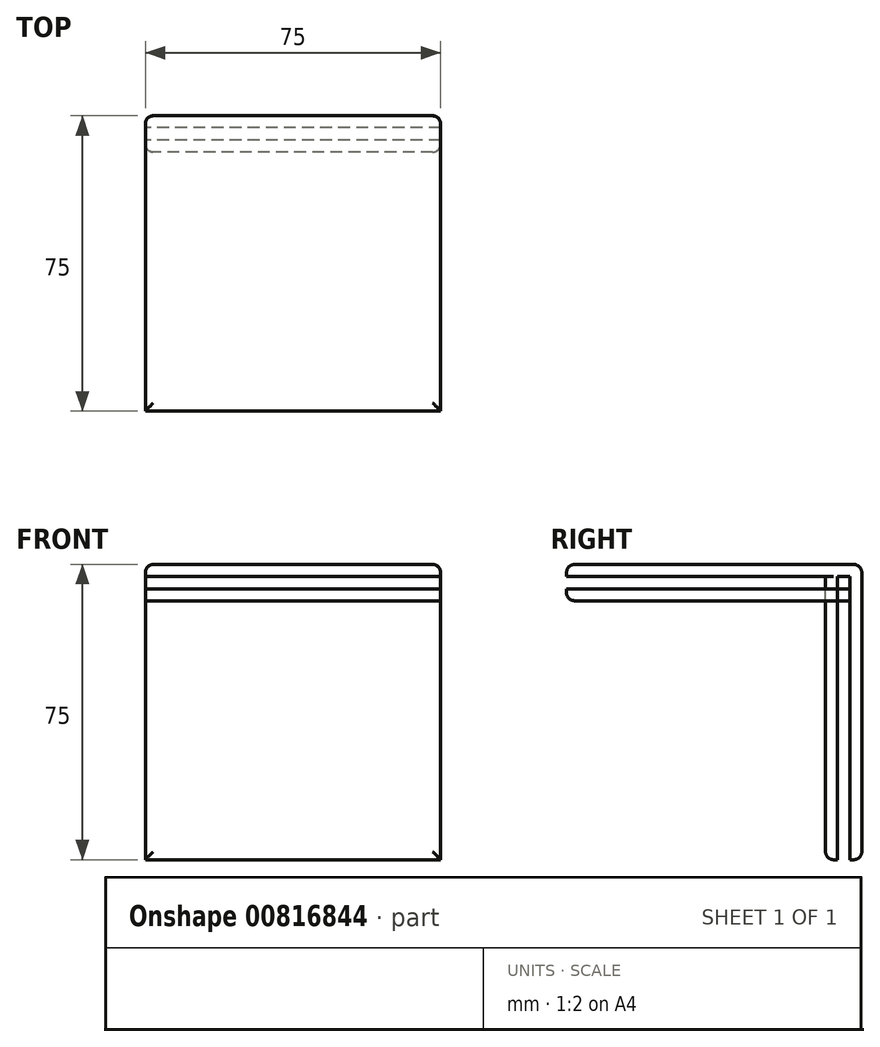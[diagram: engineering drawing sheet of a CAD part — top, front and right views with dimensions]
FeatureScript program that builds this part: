
annotation { "Feature Type Name" : "Feature", "Feature Type Description" : "" }
export const myFeature = defineFeature(function(context is Context, id is Id, definition is map)
    precondition{}
    {
        {
            var Q0;
            Q0=qCreatedBy(makeId("Top.planeOp"),FACE);
            var sketch = newSketch(context, id + "F0", { "sketchPlane" : qUnion([Q0])});
            skLineSegment(sketch, "E0.bottom", {"start": v(37.5, -37.5) * mm, "end": v(-37.5, -37.5) * mm});
            skLineSegment(sketch, "E0.top", {"start": v(37.5, 37.5) * mm, "end": v(-37.5, 37.5) * mm});
            skLineSegment(sketch, "E0.left", {"start": v(37.5, -37.5) * mm, "end": v(37.5, 37.5) * mm});
            skLineSegment(sketch, "E0.right", {"start": v(-37.5, -37.5) * mm, "end": v(-37.5, 37.5) * mm});
            skPoint(sketch, "E0.middle", {"position": v(0, 0) * mm});
            skSolve(sketch);
        }
        {
            var Q0;
            Q0=qSketchRegion(id+"F0",true);
            extrude(context, id + "F1", {"entities" : qUnion([Q0]), "depth" : 3 * mm, "offsetDistance" : 25 * mm});
        }
        {
            var Q0;
            Q0=makeQuery(id+"F1.opExtrude","SWEPT_FACE",FACE,{"disambiguationData":[OSD([sQuery(id+"F0.wireOp",EDGE,"E0.right")])]});
            var sketch = newSketch(context, id + "F2", { "sketchPlane" : qUnion([Q0])});
            skLineSegment(sketch, "E1.bottom", {"start": v(-37.5, 3) * mm, "end": v(-34.5, 3) * mm});
            skLineSegment(sketch, "E1.top", {"start": v(-37.5, -72) * mm, "end": v(-34.5, -72) * mm});
            skLineSegment(sketch, "E1.left", {"start": v(-37.5, 3) * mm, "end": v(-37.5, -72) * mm});
            skLineSegment(sketch, "E1.right", {"start": v(-34.5, 3) * mm, "end": v(-34.5, -72) * mm});
            skLineSegment(sketch, "E2.bottom", {"start": v(-31.3, 3) * mm, "end": v(-28.3, 3) * mm});
            skLineSegment(sketch, "E2.top", {"start": v(-31.3, -72) * mm, "end": v(-28.3, -72) * mm});
            skLineSegment(sketch, "E2.left", {"start": v(-31.3, 3) * mm, "end": v(-31.3, -72) * mm});
            skLineSegment(sketch, "E2.right", {"start": v(-28.3, 3) * mm, "end": v(-28.3, -72) * mm});
            skLineSegment(sketch, "E3", {"start": v(-36, -72) * mm, "end": v(-7.39, -72) * mm, "construction": true});
            skSolve(sketch);
        }
        {
            var Q0;
            Q0=qSketchRegion(id+"F2",true);
            var Q1;
            Q1=makeQuery(id+"F1.opExtrude","SWEPT_FACE",FACE,{"disambiguationData":[OSD([sQuery(id+"F0.wireOp",EDGE,"E0.left")])]});
            extrude(context, id + "F3", {"entities" : qUnion([Q0]), "operationType" : NewBodyOperationType.ADD, "endBound" : BoundingType.UP_TO_SURFACE, "oppositeDirection" : true, "depth" : 25 * mm, "endBoundEntityFace" : qUnion([Q1]), "offsetDistance" : 25 * mm});
        }
        {
            var Q0;
            Q0=makeQuery(id+"F1.opExtrude","SWEPT_FACE",FACE,{"disambiguationData":[OSD([sQuery(id+"F0.wireOp",EDGE,"E0.bottom")])]});
            var sketch = newSketch(context, id + "F4", { "sketchPlane" : qUnion([Q0])});
            skLineSegment(sketch, "E4.0", {"start": v(37.5, -3.2) * mm, "end": v(-37.5, -3.2) * mm});
            skLineSegment(sketch, "E5.bottom", {"start": v(-37.5, -3.2) * mm, "end": v(37.5, -3.2) * mm});
            skLineSegment(sketch, "E5.top", {"start": v(-37.5, -6.2) * mm, "end": v(37.5, -6.2) * mm});
            skLineSegment(sketch, "E5.left", {"start": v(-37.5, -3.2) * mm, "end": v(-37.5, -6.2) * mm});
            skLineSegment(sketch, "E5.right", {"start": v(37.5, -3.2) * mm, "end": v(37.5, -6.2) * mm});
            skLineSegment(sketch, "E6.0", {"start": v(37.5, -72) * mm, "end": v(37.5, -3.2) * mm});
            skSolve(sketch);
        }
        {
            var Q0;
            Q0=qSketchRegion(id+"F4",true);
            var Q1;
            Q1=makeQuery(id+"F3.opExtrude","SWEPT_FACE",FACE,{"disambiguationData":[OSD([sQuery(id+"F2.wireOp",EDGE,"E1.right")])]});
            extrude(context, id + "F5", {"entities" : qUnion([Q0]), "endBound" : BoundingType.UP_TO_SURFACE, "oppositeDirection" : true, "depth" : 25 * mm, "endBoundEntityFace" : qUnion([Q1]), "offsetDistance" : 25 * mm});
        }
        {
            var Q0;
            Q0=makeQuery(id+"F3.boolean.opBoolean","MERGE",FACE,{"derivedFrom":[makeQuery(id+"F1.opExtrude","SWEPT_FACE",FACE,{"disambiguationData":[OSD([sQuery(id+"F0.wireOp",EDGE,"E0.right")])]}),makeQuery(id+"F3.opExtrude","CAP_FACE",FACE,{"disambiguationData":[OSD([sQuery(id+"F2.wireOp",EDGE,"E1.bottom"),sQuery(id+"F2.wireOp",EDGE,"E1.top"),sQuery(id+"F2.wireOp",EDGE,"E1.left"),sQuery(id+"F2.wireOp",EDGE,"E1.right")])],"isStart":true}),makeQuery(id+"F3.opExtrude","CAP_FACE",FACE,{"disambiguationData":[OSD([sQuery(id+"F2.wireOp",EDGE,"E2.bottom"),sQuery(id+"F2.wireOp",EDGE,"E2.top"),sQuery(id+"F2.wireOp",EDGE,"E2.left"),sQuery(id+"F2.wireOp",EDGE,"E2.right")])],"isStart":true})]});
            var sketch = newSketch(context, id + "F6", { "sketchPlane" : qUnion([Q0])});
            skLineSegment(sketch, "E7.0", {"start": v(-34.5, -3.2) * mm, "end": v(37.5, -3.2) * mm});
            skLineSegment(sketch, "E8.bottom", {"start": v(-34.5, 0) * mm, "end": v(-31.3, 0) * mm});
            skLineSegment(sketch, "E8.top", {"start": v(-34.5, -3.2) * mm, "end": v(-31.3, -3.2) * mm});
            skLineSegment(sketch, "E8.left", {"start": v(-34.5, 0) * mm, "end": v(-34.5, -3.2) * mm});
            skLineSegment(sketch, "E8.right", {"start": v(-31.3, 0) * mm, "end": v(-31.3, -3.2) * mm});
            skSolve(sketch);
        }
        {
            var Q0;
            Q0=qSketchRegion(id+"F6",true);
            var Q1;
            Q1=makeQuery(id+"F3.boolean.opBoolean","MERGE",FACE,{"derivedFrom":[makeQuery(id+"F1.opExtrude","SWEPT_FACE",FACE,{"disambiguationData":[OSD([sQuery(id+"F0.wireOp",EDGE,"E0.left")])]}),makeQuery(id+"F3.opExtrude","CAP_FACE",FACE,{"disambiguationData":[OSD([sQuery(id+"F2.wireOp",EDGE,"E1.bottom"),sQuery(id+"F2.wireOp",EDGE,"E1.top"),sQuery(id+"F2.wireOp",EDGE,"E1.left"),sQuery(id+"F2.wireOp",EDGE,"E1.right")])],"isStart":false}),makeQuery(id+"F3.opExtrude","CAP_FACE",FACE,{"disambiguationData":[OSD([sQuery(id+"F2.wireOp",EDGE,"E2.bottom"),sQuery(id+"F2.wireOp",EDGE,"E2.top"),sQuery(id+"F2.wireOp",EDGE,"E2.left"),sQuery(id+"F2.wireOp",EDGE,"E2.right")])],"isStart":false})]});
            extrude(context, id + "F7", {"entities" : qUnion([Q0]), "endBound" : BoundingType.UP_TO_SURFACE, "oppositeDirection" : true, "depth" : 25 * mm, "endBoundEntityFace" : qUnion([Q1]), "offsetDistance" : 25 * mm});
        }
        {
            var Q0;
            Q0=makeQuery(id+"F1.opExtrude","CAP_FACE",FACE,{"disambiguationData":[OSD([sQuery(id+"F0.wireOp",EDGE,"E0.bottom"),sQuery(id+"F0.wireOp",EDGE,"E0.top"),sQuery(id+"F0.wireOp",EDGE,"E0.left"),sQuery(id+"F0.wireOp",EDGE,"E0.right")])],"isStart":false});
            var Q1;
            Q1=makeQuery(id+"F3.boolean.opBoolean","MERGE",FACE,{"derivedFrom":[makeQuery(id+"F1.opExtrude","SWEPT_FACE",FACE,{"disambiguationData":[OSD([sQuery(id+"F0.wireOp",EDGE,"E0.top")])]}),makeQuery(id+"F3.opExtrude","SWEPT_FACE",FACE,{"disambiguationData":[OSD([sQuery(id+"F2.wireOp",EDGE,"E1.left")])]})]});
            var Q2;
            Q2=makeQuery(id+"F5.opExtrude","CAP_EDGE",EDGE,{"disambiguationData":[OSD([sQuery(id+"F4.wireOp",EDGE,"E5.top")])],"isStart":true});
            var Q3;
            Q3=makeQuery(id+"F3.opExtrude","SWEPT_EDGE",EDGE,{"disambiguationData":[OSD([sQuery(id+"F2.wireOp",EDGE,"E2.top"),sQuery(id+"F2.wireOp",EDGE,"E2.right")])]});
            var Q4;
            Q4=makeQuery(id+"F3.opExtrude","CAP_EDGE",EDGE,{"disambiguationData":[OSD([sQuery(id+"F2.wireOp",EDGE,"E2.right")])],"isStart":false});
            var Q5;
            Q5=makeQuery(id+"F3.opExtrude","CAP_EDGE",EDGE,{"disambiguationData":[OSD([sQuery(id+"F2.wireOp",EDGE,"E2.right")])],"isStart":true});
            fillet(context, id + "F8", {"entities" : qUnion([Q0, Q1, Q2, Q3, Q4, Q5]), "radius" : 2 * mm, "tangentPropagation" : true, "allowEdgeOverflow" : false});
        }
    });
